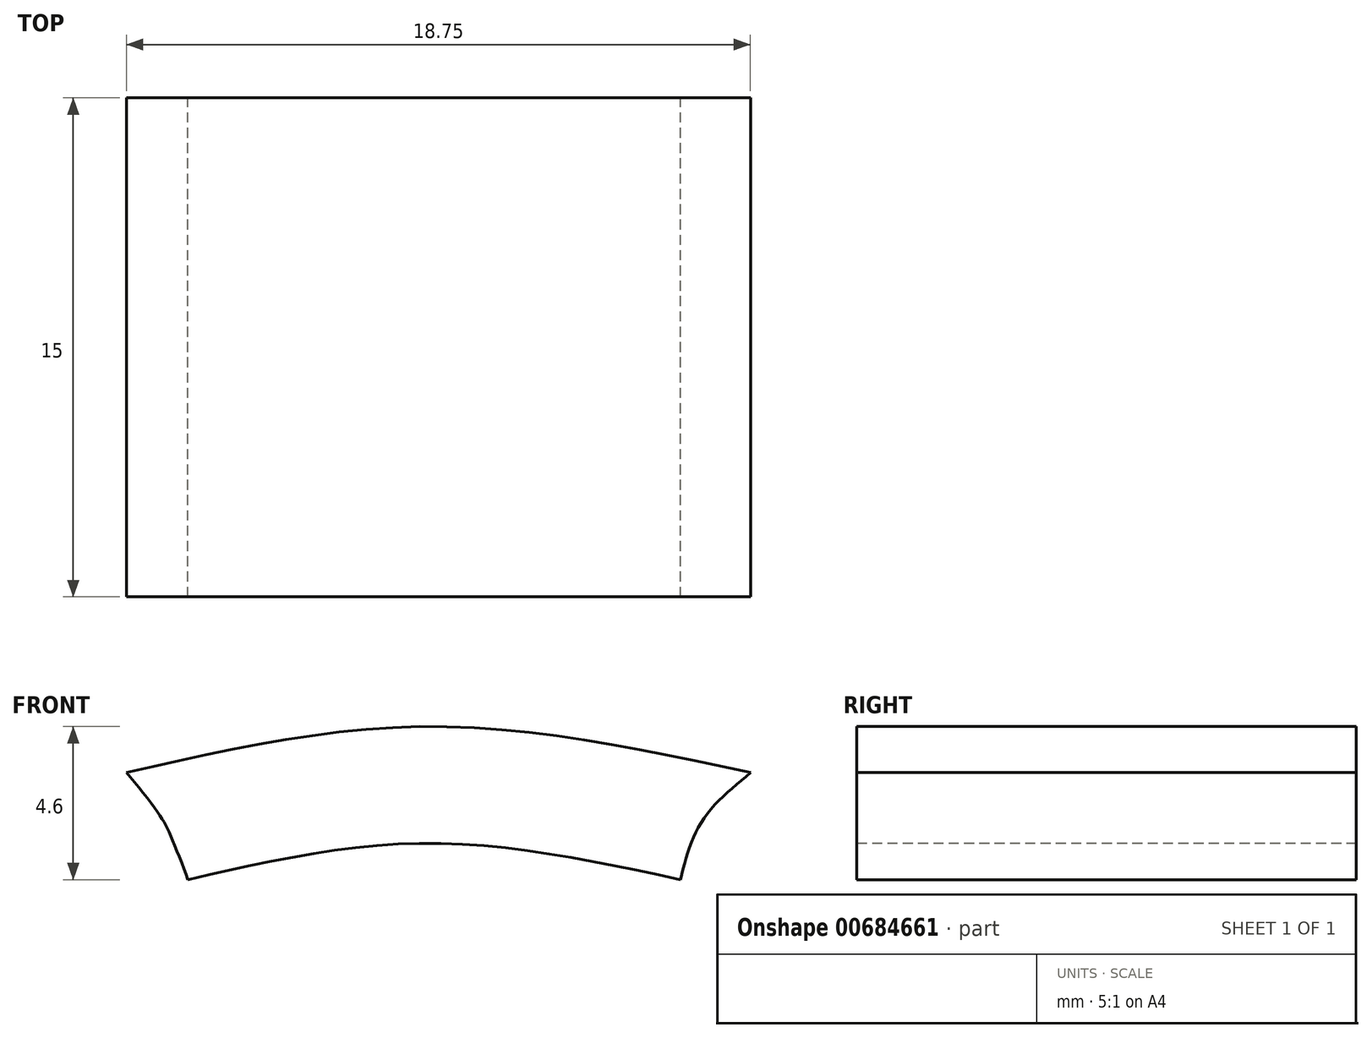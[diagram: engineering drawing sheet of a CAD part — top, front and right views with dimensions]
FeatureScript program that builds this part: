
annotation { "Feature Type Name" : "Feature", "Feature Type Description" : "" }
export const myFeature = defineFeature(function(context is Context, id is Id, definition is map)
    precondition{}
    {
        {
            var Q0;
            Q0=qCreatedBy(makeId("Front.planeOp"),FACE);
            var sketch = newSketch(context, id + "F0", { "sketchPlane" : qUnion([Q0])});
            skFitSpline(sketch, "E0", {"points": [v(-7.17, 0) * mm, v(0, 1.1) * mm, v(7.64, 0) * mm], "startDerivative": vector(14.44, 3.3) * mm, "endDerivative": vector(15.17, -3.27) * mm});
            skFitSpline(sketch, "E1", {"points": [v(-9.01, 3.22) * mm, v(0.07, 4.6) * mm, v(9.74, 3.22) * mm], "startDerivative": vector(18.3, 4.18) * mm, "endDerivative": vector(19.22, -4.14) * mm});
            skFitSpline(sketch, "E2", {"points": [v(-9.01, 3.22) * mm, v(-8.17, 2.16) * mm, v(-7.85, 1.66) * mm, v(-7.6, 1.13) * mm, v(-7.17, 0) * mm], "startDerivative": vector(2.51, -2.96) * mm, "endDerivative": vector(1.17, -3.47) * mm});
            skFitSpline(sketch, "E3", {"points": [v(9.74, 3.22) * mm, v(8.27, 1.73) * mm, v(7.64, 0) * mm], "startDerivative": vector(-3.27, -2.7) * mm, "endDerivative": vector(-0.91, -3.75) * mm});
            skSolve(sketch);
        }
        {
            var Q0;
            Q0 = qSketchRegion(id + "F0", true);
            extrude(context, id + "F1", {"entities" : qUnion([Q0]), "depth" : 15 * mm, "offsetDistance" : 25 * mm});
        }
    });
